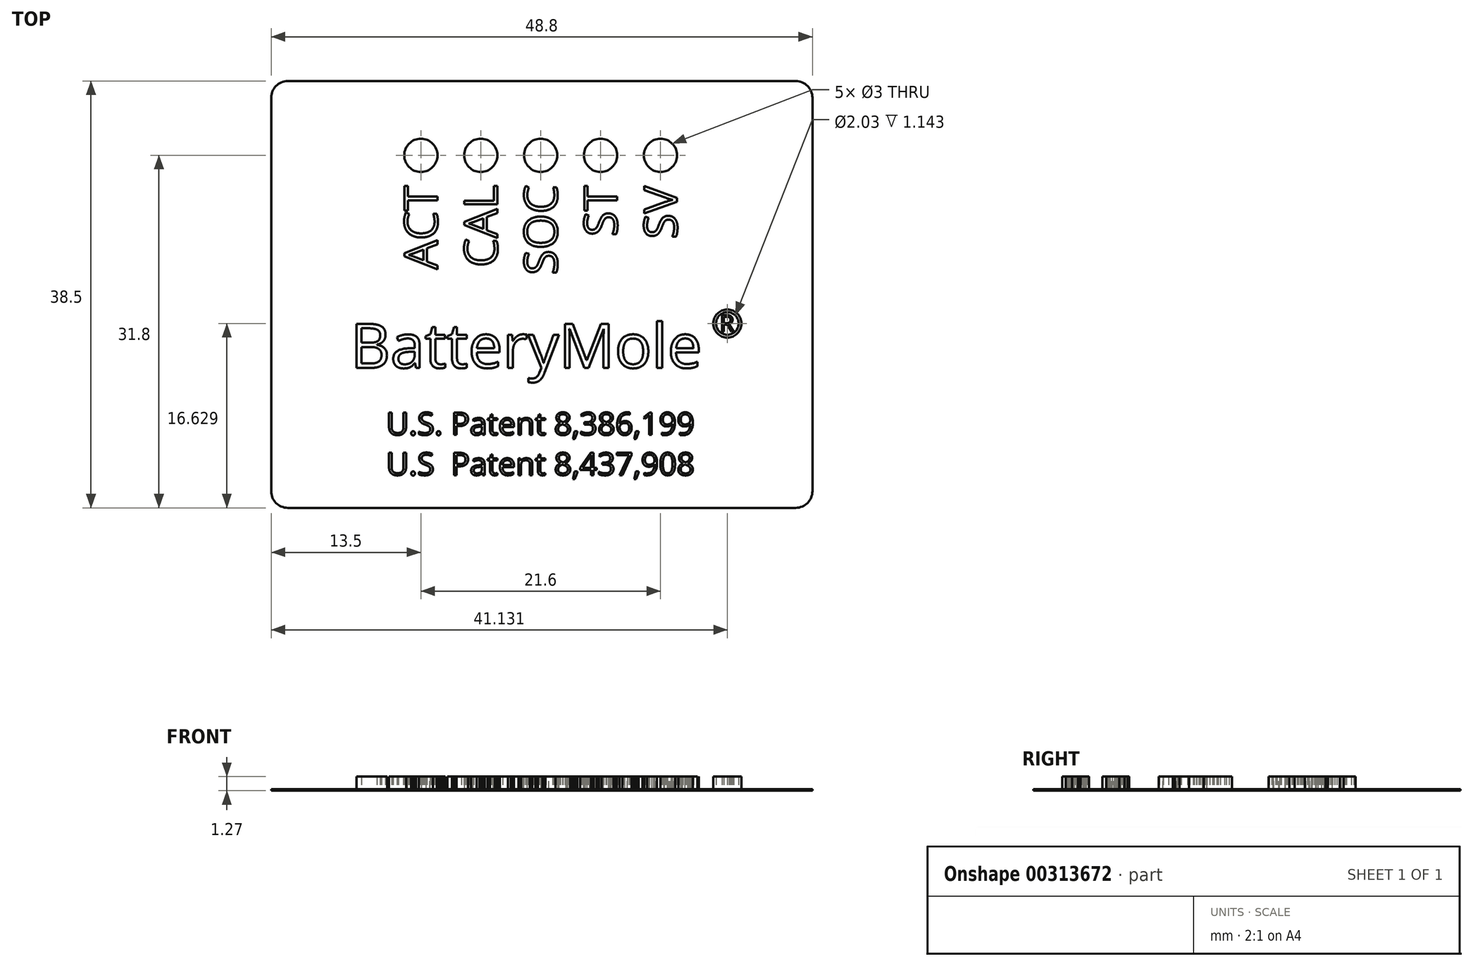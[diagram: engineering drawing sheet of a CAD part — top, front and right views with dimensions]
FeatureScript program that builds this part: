
annotation { "Feature Type Name" : "Feature", "Feature Type Description" : "" }
export const myFeature = defineFeature(function(context is Context, id is Id, definition is map)
    precondition{}
    {
        {
            var Q0;
            Q0=qCreatedBy(makeId("Top.planeOp"),FACE);
            var sketch = newSketch(context, id + "F0", { "sketchPlane" : qUnion([Q0])});
            skLineSegment(sketch, "E0.bottom", {"start": v(1.5, 38.5) * mm, "end": v(47.3, 38.5) * mm});
            skLineSegment(sketch, "E0.top", {"start": v(1.5, 0) * mm, "end": v(47.3, 0) * mm});
            skLineSegment(sketch, "E0.left", {"start": v(0, 37) * mm, "end": v(0, 1.5) * mm});
            skLineSegment(sketch, "E0.right", {"start": v(48.8, 37) * mm, "end": v(48.8, 1.5) * mm});
            skPoint(sketch, "E1.visualSharp", {"position": v(0, 38.5) * mm});
            skArc(sketch, "E1.filletArc", {"start": v(1.5, 38.5) * mm, "mid": v(0.44, 38.06) * mm, "end": v(0, 37) * mm});
            skPoint(sketch, "E2.visualSharp", {"position": v(48.8, 38.5) * mm});
            skArc(sketch, "E2.filletArc", {"start": v(48.8, 37) * mm, "mid": v(48.36, 38.06) * mm, "end": v(47.3, 38.5) * mm});
            skPoint(sketch, "E3.visualSharp", {"position": v(48.8, 0) * mm});
            skArc(sketch, "E3.filletArc", {"start": v(47.3, 0) * mm, "mid": v(48.36, 0.44) * mm, "end": v(48.8, 1.5) * mm});
            skPoint(sketch, "E4.visualSharp", {"position": v(0, 0) * mm});
            skArc(sketch, "E4.filletArc", {"start": v(0, 1.5) * mm, "mid": v(0.44, 0.44) * mm, "end": v(1.5, 0) * mm});
            skLineSegment(sketch, "E5", {"start": v(-1.94, 31.8) * mm, "end": v(50.94, 31.8) * mm, "construction": true});
            skPoint(sketch, "E6", {"position": v(0, 19.25) * mm});
            skCircle(sketch, "E7", {"center": v(13.5, 31.8) * mm, "radius": 1.5 * mm});
            skCircle(sketch, "E8", {"center": v(18.9, 31.8) * mm, "radius": 1.5 * mm});
            skCircle(sketch, "E9", {"center": v(24.3, 31.8) * mm, "radius": 1.5 * mm});
            skCircle(sketch, "E10", {"center": v(29.7, 31.8) * mm, "radius": 1.5 * mm});
            skCircle(sketch, "E11", {"center": v(35.1, 31.8) * mm, "radius": 1.5 * mm});
            skLineSegment(sketch, "E12", {"start": v(24.3, 31.8) * mm, "end": v(24.3, 57.95) * mm, "construction": true});
            skLineSegment(sketch, "E13", {"start": v(41.58, 29.3) * mm, "end": v(3.43, 29.3) * mm, "construction": true});
            skSolve(sketch);
        }
        {
            var Q0;
            Q0=qCreatedBy(makeId("Top.planeOp"),FACE);
            var sketch = newSketch(context, id + "F1", { "sketchPlane" : qUnion([Q0])});
            skLineSegment(sketch, "E14.bottom", {"start": v(1.5, 38.5) * mm, "end": v(47.3, 38.5) * mm});
            skLineSegment(sketch, "E14.top", {"start": v(1.5, 0) * mm, "end": v(47.3, 0) * mm});
            skLineSegment(sketch, "E14.left", {"start": v(0, 37) * mm, "end": v(0, 1.5) * mm});
            skLineSegment(sketch, "E14.right", {"start": v(48.8, 37) * mm, "end": v(48.8, 1.5) * mm});
            skPoint(sketch, "E15.visualSharp", {"position": v(0, 38.5) * mm});
            skArc(sketch, "E15.filletArc", {"start": v(1.5, 38.5) * mm, "mid": v(0.44, 38.06) * mm, "end": v(0, 37) * mm});
            skPoint(sketch, "E16.visualSharp", {"position": v(48.8, 38.5) * mm});
            skArc(sketch, "E16.filletArc", {"start": v(48.8, 37) * mm, "mid": v(48.36, 38.06) * mm, "end": v(47.3, 38.5) * mm});
            skPoint(sketch, "E17.visualSharp", {"position": v(48.8, 0) * mm});
            skArc(sketch, "E17.filletArc", {"start": v(47.3, 0) * mm, "mid": v(48.36, 0.44) * mm, "end": v(48.8, 1.5) * mm});
            skPoint(sketch, "E18.visualSharp", {"position": v(0, 0) * mm});
            skArc(sketch, "E18.filletArc", {"start": v(0, 1.5) * mm, "mid": v(0.44, 0.44) * mm, "end": v(1.5, 0) * mm});
            skText(sketch, "E19", { "text": "BatteryMole", "fontName": "OpenSans-Regular.ttf"});
            skCircle(sketch, "E20", {"center": v(41.13, 16.63) * mm, "radius": 1.02 * mm});
            skCircle(sketch, "E21", {"center": v(41.13, 16.63) * mm, "radius": 1.27 * mm});
            skText(sketch, "E22", { "text": "U.S. Patent 8,386,199", "fontName": "OpenSans-Regular.ttf"});
            skText(sketch, "E23", { "text": "U.S. Patent 8,437,908", "fontName": "OpenSans-Regular.ttf"});
            skPoint(sketch, "E24", {"position": v(0, 19.25) * mm});
            skLineSegment(sketch, "E25", {"start": v(24.3, 16.46) * mm, "end": v(24.3, 31.8) * mm, "construction": true});
            skText(sketch, "E26", { "text": "ACT", "fontName": "OpenSans-Regular.ttf"});
            skText(sketch, "E27", { "text": "CAL", "fontName": "OpenSans-Regular.ttf"});
            skText(sketch, "E28", { "text": "SV", "fontName": "OpenSans-Regular.ttf"});
            skText(sketch, "E29", { "text": "ST", "fontName": "OpenSans-Regular.ttf"});
            skLineSegment(sketch, "E30", {"start": v(41.58, 29.3) * mm, "end": v(3.43, 29.3) * mm, "construction": true});
            skText(sketch, "E31", { "text": "R", "fontName": "OpenSans-Regular.ttf"});
            skText(sketch, "E32", { "text": "SOC", "fontName": "OpenSans-Regular.ttf"});
            skPoint(sketch, "E33", {"position": v(24.3, 21) * mm});
            const initialGuessF1  = {"E19": [0.00715, 0.01263, 1, 0, 0.004], "E22": [0.01037, 0.00658, 1, 0, 0.00203], "E23": [0.01037, 0.00295, 1, 0, 0.00203], "E26": [0.015, 0.0215, 0, 1, 0.003], "E27": [0.0204, 0.0217, 0, 1, 0.003], "E28": [0.0366, 0.02426, 0, 1, 0.003], "E29": [0.0312, 0.02448, 0, 1, 0.003], "E31": [0.04045, 0.0159, 1, 0, 0.0015], "E32": [0.0258, 0.021, 0, 1, 0.003]};
            skSetInitialGuess(sketch, initialGuessF1);
            skSolve(sketch);
        }
        {
            var Q0;
            Q0=makeQuery(id+"F0.imprint","IMPRINT",FACE,{"disambiguationData":[TD([[makeQuery(id+"F0.imprint","IMPRINT",EDGE,{"derivedFrom":sQuery(id+"F0.wireOp",EDGE,"E0.bottom")}),-1.0]])]});
            extrude(context, id + "F2", {"entities" : qUnion([Q0]), "depth" : 0.13 * mm});
        }
        {
            var Q0;
            Q0=makeQuery(id+"F1.imprint","IMPRINT",FACE,{"disambiguationData":[TD([[makeQuery(id+"F1.imprint","IMPRINT",EDGE,{"derivedFrom":sQuery(id+"F1.wireOp",EDGE,"E22.sketch_text.stroke-0")}),-1.0]])]});
            var Q1;
            Q1=makeQuery(id+"F1.imprint","IMPRINT",FACE,{"disambiguationData":[TD([[makeQuery(id+"F1.imprint","IMPRINT",EDGE,{"derivedFrom":sQuery(id+"F1.wireOp",EDGE,"E22.sketch_text.stroke-14")}),-1.0]])]});
            var Q2;
            Q2=makeQuery(id+"F1.imprint","IMPRINT",FACE,{"disambiguationData":[TD([[makeQuery(id+"F1.imprint","IMPRINT",EDGE,{"derivedFrom":sQuery(id+"F1.wireOp",EDGE,"E22.sketch_text.stroke-22")}),-1.0]])]});
            var Q3;
            Q3=makeQuery(id+"F1.imprint","IMPRINT",FACE,{"disambiguationData":[TD([[makeQuery(id+"F1.imprint","IMPRINT",EDGE,{"derivedFrom":sQuery(id+"F1.wireOp",EDGE,"E22.sketch_text.stroke-47")}),-1.0]])]});
            var Q4;
            Q4=makeQuery(id+"F1.imprint","IMPRINT",FACE,{"disambiguationData":[TD([[makeQuery(id+"F1.imprint","IMPRINT",EDGE,{"derivedFrom":sQuery(id+"F1.wireOp",EDGE,"E22.sketch_text.stroke-55")}),-1.0]])]});
            var Q5;
            Q5=makeQuery(id+"F1.imprint","IMPRINT",FACE,{"disambiguationData":[TD([[makeQuery(id+"F1.imprint","IMPRINT",EDGE,{"derivedFrom":sQuery(id+"F1.wireOp",EDGE,"E22.sketch_text.stroke-70")}),-1.0]])]});
            var Q6;
            Q6=makeQuery(id+"F1.imprint","IMPRINT",FACE,{"disambiguationData":[TD([[makeQuery(id+"F1.imprint","IMPRINT",EDGE,{"derivedFrom":sQuery(id+"F1.wireOp",EDGE,"E22.sketch_text.stroke-97")}),-1.0]])]});
            var Q7;
            Q7=makeQuery(id+"F1.imprint","IMPRINT",FACE,{"disambiguationData":[TD([[makeQuery(id+"F1.imprint","IMPRINT",EDGE,{"derivedFrom":sQuery(id+"F1.wireOp",EDGE,"E22.sketch_text.stroke-116")}),-1.0]])]});
            var Q8;
            Q8=makeQuery(id+"F1.imprint","IMPRINT",FACE,{"disambiguationData":[TD([[makeQuery(id+"F1.imprint","IMPRINT",EDGE,{"derivedFrom":sQuery(id+"F1.wireOp",EDGE,"E22.sketch_text.stroke-135")}),-1.0]])]});
            var Q9;
            Q9=makeQuery(id+"F1.imprint","IMPRINT",FACE,{"disambiguationData":[TD([[makeQuery(id+"F1.imprint","IMPRINT",EDGE,{"derivedFrom":sQuery(id+"F1.wireOp",EDGE,"E23.sketch_text.stroke-152")}),-1.0]])]});
            var Q10;
            Q10=makeQuery(id+"F1.imprint","IMPRINT",FACE,{"disambiguationData":[TD([[makeQuery(id+"F1.imprint","IMPRINT",EDGE,{"derivedFrom":sQuery(id+"F1.wireOp",EDGE,"E23.sketch_text.stroke-135")}),-1.0]])]});
            var Q11;
            Q11=makeQuery(id+"F1.imprint","IMPRINT",FACE,{"disambiguationData":[TD([[makeQuery(id+"F1.imprint","IMPRINT",EDGE,{"derivedFrom":sQuery(id+"F1.wireOp",EDGE,"E23.sketch_text.stroke-116")}),-1.0]])]});
            var Q12;
            Q12=makeQuery(id+"F1.imprint","IMPRINT",FACE,{"disambiguationData":[TD([[makeQuery(id+"F1.imprint","IMPRINT",EDGE,{"derivedFrom":sQuery(id+"F1.wireOp",EDGE,"E23.sketch_text.stroke-97")}),-1.0]])]});
            var Q13;
            Q13=makeQuery(id+"F1.imprint","IMPRINT",FACE,{"disambiguationData":[TD([[makeQuery(id+"F1.imprint","IMPRINT",EDGE,{"derivedFrom":sQuery(id+"F1.wireOp",EDGE,"E23.sketch_text.stroke-70")}),-1.0]])]});
            var Q14;
            Q14=makeQuery(id+"F1.imprint","IMPRINT",FACE,{"disambiguationData":[TD([[makeQuery(id+"F1.imprint","IMPRINT",EDGE,{"derivedFrom":sQuery(id+"F1.wireOp",EDGE,"E23.sketch_text.stroke-55")}),-1.0]])]});
            var Q15;
            Q15=makeQuery(id+"F1.imprint","IMPRINT",FACE,{"disambiguationData":[TD([[makeQuery(id+"F1.imprint","IMPRINT",EDGE,{"derivedFrom":sQuery(id+"F1.wireOp",EDGE,"E23.sketch_text.stroke-0")}),-1.0]])]});
            var Q16;
            Q16=makeQuery(id+"F1.imprint","IMPRINT",FACE,{"disambiguationData":[TD([[makeQuery(id+"F1.imprint","IMPRINT",EDGE,{"derivedFrom":sQuery(id+"F1.wireOp",EDGE,"E23.sketch_text.stroke-14")}),-1.0]])]});
            var Q17;
            Q17=makeQuery(id+"F1.imprint","IMPRINT",FACE,{"disambiguationData":[TD([[makeQuery(id+"F1.imprint","IMPRINT",EDGE,{"derivedFrom":sQuery(id+"F1.wireOp",EDGE,"E23.sketch_text.stroke-22")}),-1.0]])]});
            var Q18;
            Q18=makeQuery(id+"F1.imprint","IMPRINT",FACE,{"disambiguationData":[TD([[makeQuery(id+"F1.imprint","IMPRINT",EDGE,{"derivedFrom":sQuery(id+"F1.wireOp",EDGE,"E23.sketch_text.stroke-310")}),-1.0]])]});
            var Q19;
            Q19=makeQuery(id+"F1.imprint","IMPRINT",FACE,{"disambiguationData":[TD([[makeQuery(id+"F1.imprint","IMPRINT",EDGE,{"derivedFrom":sQuery(id+"F1.wireOp",EDGE,"E23.sketch_text.stroke-294")}),-1.0]])]});
            var Q20;
            Q20=makeQuery(id+"F1.imprint","IMPRINT",FACE,{"disambiguationData":[TD([[makeQuery(id+"F1.imprint","IMPRINT",EDGE,{"derivedFrom":sQuery(id+"F1.wireOp",EDGE,"E23.sketch_text.stroke-268")}),-1.0]])]});
            var Q21;
            Q21=makeQuery(id+"F1.imprint","IMPRINT",FACE,{"disambiguationData":[TD([[makeQuery(id+"F1.imprint","IMPRINT",EDGE,{"derivedFrom":sQuery(id+"F1.wireOp",EDGE,"E23.sketch_text.stroke-261")}),-1.0]])]});
            var Q22;
            Q22=makeQuery(id+"F1.imprint","IMPRINT",FACE,{"disambiguationData":[TD([[makeQuery(id+"F1.imprint","IMPRINT",EDGE,{"derivedFrom":sQuery(id+"F1.wireOp",EDGE,"E23.sketch_text.stroke-254")}),-1.0]])]});
            var Q23;
            Q23=makeQuery(id+"F1.imprint","IMPRINT",FACE,{"disambiguationData":[TD([[makeQuery(id+"F1.imprint","IMPRINT",EDGE,{"derivedFrom":sQuery(id+"F1.wireOp",EDGE,"E23.sketch_text.stroke-226")}),-1.0]])]});
            var Q24;
            Q24=makeQuery(id+"F1.imprint","IMPRINT",FACE,{"disambiguationData":[TD([[makeQuery(id+"F1.imprint","IMPRINT",EDGE,{"derivedFrom":sQuery(id+"F1.wireOp",EDGE,"E23.sketch_text.stroke-209")}),-1.0]])]});
            var Q25;
            Q25=makeQuery(id+"F1.imprint","IMPRINT",FACE,{"disambiguationData":[TD([[makeQuery(id+"F1.imprint","IMPRINT",EDGE,{"derivedFrom":sQuery(id+"F1.wireOp",EDGE,"E22.sketch_text.stroke-209")}),-1.0]])]});
            var Q26;
            Q26=makeQuery(id+"F1.imprint","IMPRINT",FACE,{"disambiguationData":[TD([[makeQuery(id+"F1.imprint","IMPRINT",EDGE,{"derivedFrom":sQuery(id+"F1.wireOp",EDGE,"E22.sketch_text.stroke-237")}),-1.0]])]});
            var Q27;
            Q27=makeQuery(id+"F1.imprint","IMPRINT",FACE,{"disambiguationData":[TD([[makeQuery(id+"F1.imprint","IMPRINT",EDGE,{"derivedFrom":sQuery(id+"F1.wireOp",EDGE,"E22.sketch_text.stroke-268")}),-1.0]])]});
            var Q28;
            Q28=makeQuery(id+"F1.imprint","IMPRINT",FACE,{"disambiguationData":[TD([[makeQuery(id+"F1.imprint","IMPRINT",EDGE,{"derivedFrom":sQuery(id+"F1.wireOp",EDGE,"E22.sketch_text.stroke-300")}),-1.0]])]});
            var Q29;
            Q29=makeQuery(id+"F1.imprint","IMPRINT",FACE,{"disambiguationData":[TD([[makeQuery(id+"F1.imprint","IMPRINT",EDGE,{"derivedFrom":sQuery(id+"F1.wireOp",EDGE,"E22.sketch_text.stroke-309")}),-1.0]])]});
            var Q30;
            Q30=makeQuery(id+"F1.imprint","IMPRINT",FACE,{"disambiguationData":[TD([[makeQuery(id+"F1.imprint","IMPRINT",EDGE,{"derivedFrom":sQuery(id+"F1.wireOp",EDGE,"E22.sketch_text.stroke-335")}),-1.0]])]});
            var Q31;
            Q31=makeQuery(id+"F1.imprint","IMPRINT",FACE,{"disambiguationData":[TD([[makeQuery(id+"F1.imprint","IMPRINT",EDGE,{"derivedFrom":sQuery(id+"F1.wireOp",EDGE,"E22.sketch_text.stroke-293")}),-1.0]])]});
            var Q32;
            Q32=makeQuery(id+"F1.imprint","IMPRINT",FACE,{"disambiguationData":[TD([[makeQuery(id+"F1.imprint","IMPRINT",EDGE,{"derivedFrom":sQuery(id+"F1.wireOp",EDGE,"E22.sketch_text.stroke-202")}),-1.0]])]});
            var Q33;
            Q33=makeQuery(id+"F1.imprint","IMPRINT",FACE,{"disambiguationData":[TD([[makeQuery(id+"F1.imprint","IMPRINT",EDGE,{"derivedFrom":sQuery(id+"F1.wireOp",EDGE,"E22.sketch_text.stroke-171")}),-1.0]])]});
            var Q34;
            Q34=makeQuery(id+"F1.imprint","IMPRINT",FACE,{"disambiguationData":[TD([[makeQuery(id+"F1.imprint","IMPRINT",EDGE,{"derivedFrom":sQuery(id+"F1.wireOp",EDGE,"E22.sketch_text.stroke-152")}),-1.0]])]});
            var Q35;
            Q35=makeQuery(id+"F1.imprint","IMPRINT",FACE,{"disambiguationData":[TD([[makeQuery(id+"F1.imprint","IMPRINT",EDGE,{"derivedFrom":sQuery(id+"F1.wireOp",EDGE,"E23.sketch_text.stroke-202")}),-1.0]])]});
            var Q36;
            Q36=makeQuery(id+"F1.imprint","IMPRINT",FACE,{"disambiguationData":[TD([[makeQuery(id+"F1.imprint","IMPRINT",EDGE,{"derivedFrom":sQuery(id+"F1.wireOp",EDGE,"E23.sketch_text.stroke-171")}),-1.0]])]});
            var Q37;
            Q37=makeQuery(id+"F1.imprint","IMPRINT",FACE,{"disambiguationData":[TD([[makeQuery(id+"F1.imprint","IMPRINT",EDGE,{"derivedFrom":sQuery(id+"F1.wireOp",EDGE,"E19.sketch_text.stroke-0")}),-1.0]])]});
            var Q38;
            Q38=makeQuery(id+"F1.imprint","IMPRINT",FACE,{"disambiguationData":[TD([[makeQuery(id+"F1.imprint","IMPRINT",EDGE,{"derivedFrom":sQuery(id+"F1.wireOp",EDGE,"E19.sketch_text.stroke-25")}),-1.0]])]});
            var Q39;
            Q39=makeQuery(id+"F1.imprint","IMPRINT",FACE,{"disambiguationData":[TD([[makeQuery(id+"F1.imprint","IMPRINT",EDGE,{"derivedFrom":sQuery(id+"F1.wireOp",EDGE,"E19.sketch_text.stroke-52")}),-1.0]])]});
            var Q40;
            Q40=makeQuery(id+"F1.imprint","IMPRINT",FACE,{"disambiguationData":[TD([[makeQuery(id+"F1.imprint","IMPRINT",EDGE,{"derivedFrom":sQuery(id+"F1.wireOp",EDGE,"E19.sketch_text.stroke-71")}),-1.0]])]});
            var Q41;
            Q41=makeQuery(id+"F1.imprint","IMPRINT",FACE,{"disambiguationData":[TD([[makeQuery(id+"F1.imprint","IMPRINT",EDGE,{"derivedFrom":sQuery(id+"F1.wireOp",EDGE,"E19.sketch_text.stroke-90")}),-1.0]])]});
            var Q42;
            Q42=makeQuery(id+"F1.imprint","IMPRINT",FACE,{"disambiguationData":[TD([[makeQuery(id+"F1.imprint","IMPRINT",EDGE,{"derivedFrom":sQuery(id+"F1.wireOp",EDGE,"E19.sketch_text.stroke-109")}),-1.0]])]});
            var Q43;
            Q43=makeQuery(id+"F1.imprint","IMPRINT",FACE,{"disambiguationData":[TD([[makeQuery(id+"F1.imprint","IMPRINT",EDGE,{"derivedFrom":sQuery(id+"F1.wireOp",EDGE,"E19.sketch_text.stroke-122")}),-1.0]])]});
            var Q44;
            Q44=makeQuery(id+"F1.imprint","IMPRINT",FACE,{"disambiguationData":[TD([[makeQuery(id+"F1.imprint","IMPRINT",EDGE,{"derivedFrom":sQuery(id+"F1.wireOp",EDGE,"E19.sketch_text.stroke-138")}),-1.0]])]});
            var Q45;
            Q45=makeQuery(id+"F1.imprint","IMPRINT",FACE,{"disambiguationData":[TD([[makeQuery(id+"F1.imprint","IMPRINT",EDGE,{"derivedFrom":sQuery(id+"F1.wireOp",EDGE,"E19.sketch_text.stroke-156")}),-1.0]])]});
            var Q46;
            Q46=makeQuery(id+"F1.imprint","IMPRINT",FACE,{"disambiguationData":[TD([[makeQuery(id+"F1.imprint","IMPRINT",EDGE,{"derivedFrom":sQuery(id+"F1.wireOp",EDGE,"E19.sketch_text.stroke-173")}),-1.0]])]});
            var Q47;
            Q47=makeQuery(id+"F1.imprint","IMPRINT",FACE,{"disambiguationData":[TD([[makeQuery(id+"F1.imprint","IMPRINT",EDGE,{"derivedFrom":sQuery(id+"F1.wireOp",EDGE,"E19.sketch_text.stroke-177")}),-1.0]])]});
            var Q48;
            Q48=makeQuery(id+"F1.imprint","IMPRINT",FACE,{"disambiguationData":[TD([[makeQuery(id+"F1.imprint","IMPRINT",EDGE,{"derivedFrom":sQuery(id+"F1.wireOp",EDGE,"E31.sketch_text.stroke-0")}),-1.0]])]});
            var Q49;
            Q49=makeQuery(id+"F1.imprint","IMPRINT",FACE,{"disambiguationData":[TD([[makeQuery(id+"F1.imprint","IMPRINT",EDGE,{"derivedFrom":sQuery(id+"F1.wireOp",EDGE,"E20")}),-1.0]])]});
            var Q50;
            Q50=makeQuery(id+"F1.imprint","IMPRINT",FACE,{"disambiguationData":[TD([[makeQuery(id+"F1.imprint","IMPRINT",EDGE,{"derivedFrom":sQuery(id+"F1.wireOp",EDGE,"E26.sketch_text.stroke-0")}),-1.0]])]});
            var Q51;
            Q51=makeQuery(id+"F1.imprint","IMPRINT",FACE,{"disambiguationData":[TD([[makeQuery(id+"F1.imprint","IMPRINT",EDGE,{"derivedFrom":sQuery(id+"F1.wireOp",EDGE,"E27.sketch_text.stroke-0")}),-1.0]])]});
            var Q52;
            Q52=makeQuery(id+"F1.imprint","IMPRINT",FACE,{"disambiguationData":[TD([[makeQuery(id+"F1.imprint","IMPRINT",EDGE,{"derivedFrom":sQuery(id+"F1.wireOp",EDGE,"E32.sketch_text.stroke-0")}),-1.0]])]});
            var Q53;
            Q53=makeQuery(id+"F1.imprint","IMPRINT",FACE,{"disambiguationData":[TD([[makeQuery(id+"F1.imprint","IMPRINT",EDGE,{"derivedFrom":sQuery(id+"F1.wireOp",EDGE,"E32.sketch_text.stroke-25")}),-1.0]])]});
            var Q54;
            Q54=makeQuery(id+"F1.imprint","IMPRINT",FACE,{"disambiguationData":[TD([[makeQuery(id+"F1.imprint","IMPRINT",EDGE,{"derivedFrom":sQuery(id+"F1.wireOp",EDGE,"E27.sketch_text.stroke-15")}),-1.0]])]});
            var Q55;
            Q55=makeQuery(id+"F1.imprint","IMPRINT",FACE,{"disambiguationData":[TD([[makeQuery(id+"F1.imprint","IMPRINT",EDGE,{"derivedFrom":sQuery(id+"F1.wireOp",EDGE,"E26.sketch_text.stroke-13")}),-1.0]])]});
            var Q56;
            Q56=makeQuery(id+"F1.imprint","IMPRINT",FACE,{"disambiguationData":[TD([[makeQuery(id+"F1.imprint","IMPRINT",EDGE,{"derivedFrom":sQuery(id+"F1.wireOp",EDGE,"E29.sketch_text.stroke-0")}),-1.0]])]});
            var Q57;
            Q57=makeQuery(id+"F1.imprint","IMPRINT",FACE,{"disambiguationData":[TD([[makeQuery(id+"F1.imprint","IMPRINT",EDGE,{"derivedFrom":sQuery(id+"F1.wireOp",EDGE,"E29.sketch_text.stroke-25")}),-1.0]])]});
            var Q58;
            Q58=makeQuery(id+"F1.imprint","IMPRINT",FACE,{"disambiguationData":[TD([[makeQuery(id+"F1.imprint","IMPRINT",EDGE,{"derivedFrom":sQuery(id+"F1.wireOp",EDGE,"E28.sketch_text.stroke-0")}),-1.0]])]});
            var Q59;
            Q59=makeQuery(id+"F1.imprint","IMPRINT",FACE,{"disambiguationData":[TD([[makeQuery(id+"F1.imprint","IMPRINT",EDGE,{"derivedFrom":sQuery(id+"F1.wireOp",EDGE,"E28.sketch_text.stroke-25")}),-1.0]])]});
            var Q60;
            Q60=makeQuery(id+"F1.imprint","IMPRINT",FACE,{"disambiguationData":[TD([[makeQuery(id+"F1.imprint","IMPRINT",EDGE,{"derivedFrom":sQuery(id+"F1.wireOp",EDGE,"E32.sketch_text.stroke-41")}),-1.0]])]});
            var Q61;
            Q61=makeQuery(id+"F1.imprint","IMPRINT",FACE,{"disambiguationData":[TD([[makeQuery(id+"F1.imprint","IMPRINT",EDGE,{"derivedFrom":sQuery(id+"F1.wireOp",EDGE,"E27.sketch_text.stroke-28")}),-1.0]])]});
            var Q62;
            Q62=makeQuery(id+"F1.imprint","IMPRINT",FACE,{"disambiguationData":[TD([[makeQuery(id+"F1.imprint","IMPRINT",EDGE,{"derivedFrom":sQuery(id+"F1.wireOp",EDGE,"E26.sketch_text.stroke-28")}),-1.0]])]});
            extrude(context, id + "F3", {"entities" : qUnion([Q0, Q1, Q2, Q3, Q4, Q5, Q6, Q7, Q8, Q9, Q10, Q11, Q12, Q13, Q14, Q15, Q16, Q17, Q18, Q19, Q20, Q21, Q22, Q23, Q24, Q25, Q26, Q27, Q28, Q29, Q30, Q31, Q32, Q33, Q34, Q35, Q36, Q37, Q38, Q39, Q40, Q41, Q42, Q43, Q44, Q45, Q46, Q47, Q48, Q49, Q50, Q51, Q52, Q53, Q54, Q55, Q56, Q57, Q58, Q59, Q60, Q61, Q62]), "operationType" : NewBodyOperationType.ADD, "depth" : 1.27 * mm});
        }
    });
